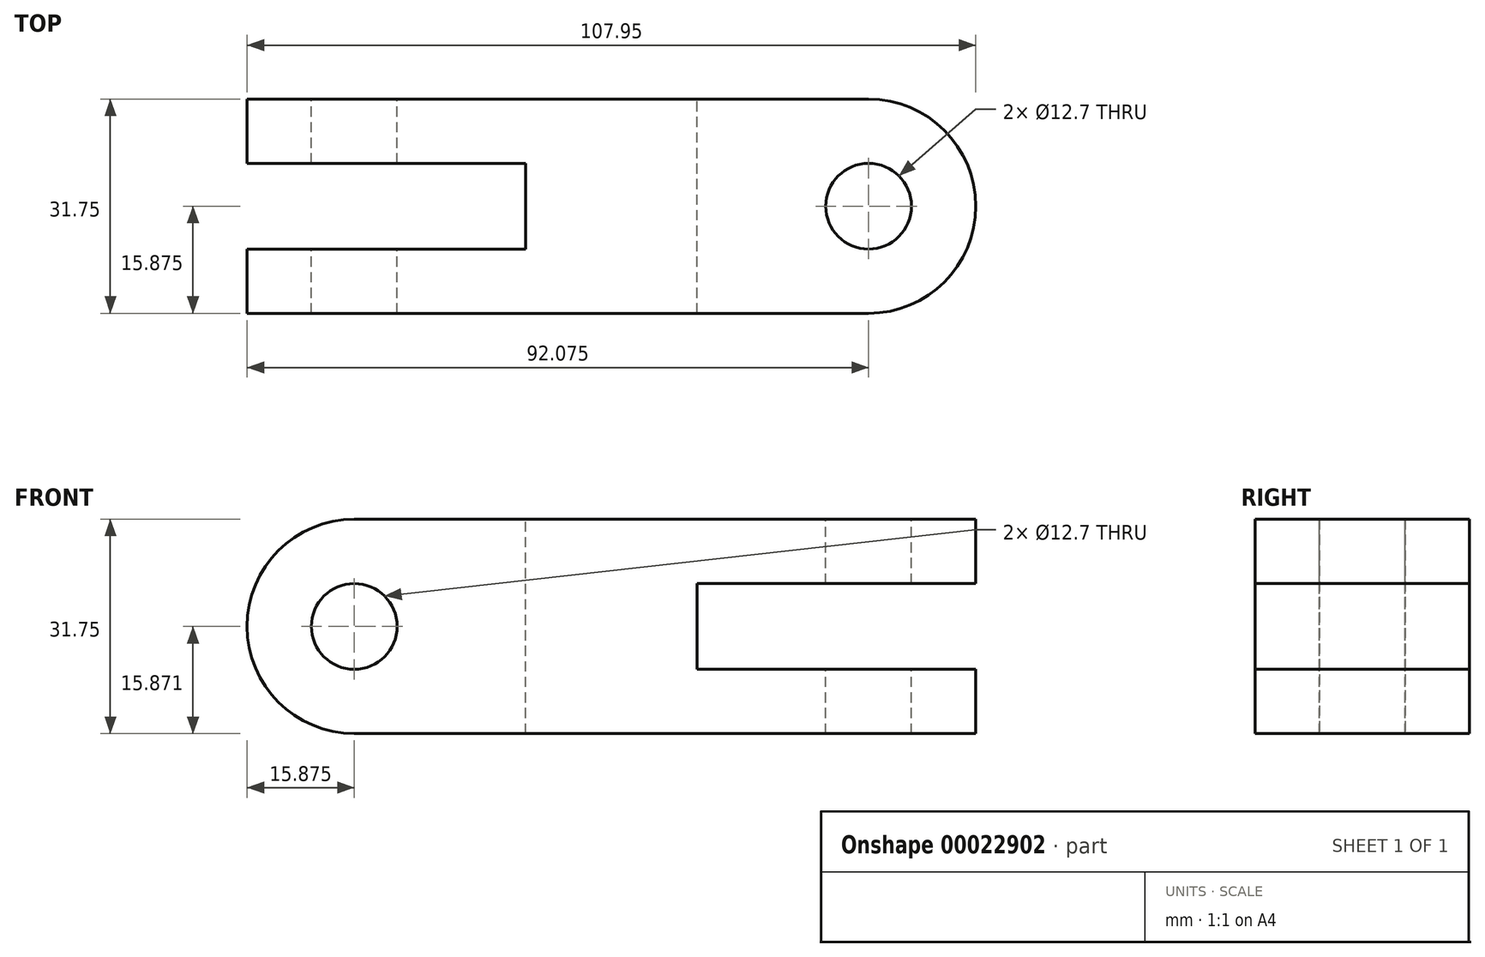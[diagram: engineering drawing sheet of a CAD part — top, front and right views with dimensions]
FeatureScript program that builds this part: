
annotation { "Feature Type Name" : "Feature", "Feature Type Description" : "" }
export const myFeature = defineFeature(function(context is Context, id is Id, definition is map)
    precondition{}
    {
        {
            var Q0;
            Q0=qCreatedBy(makeId("Front.planeOp"),FACE);
            var sketch = newSketch(context, id + "F0", { "sketchPlane" : qUnion([Q0])});
            skLineSegment(sketch, "E0.bottom", {"start": v(-92.08, 13.6) * mm, "end": v(0, 13.6) * mm});
            skLineSegment(sketch, "E0.top", {"start": v(-92.08, -18.14) * mm, "end": v(0, -18.14) * mm});
            skArc(sketch, "E1", {"start": v(-92.08, 13.6) * mm, "mid": v(-107.95, -2.27) * mm, "end": v(-92.08, -18.14) * mm});
            skCircle(sketch, "E2", {"center": v(-92.08, -2.27) * mm, "radius": 6.35 * mm});
            skLineSegment(sketch, "E3", {"start": v(0, 13.6) * mm, "end": v(0, 4.08) * mm});
            skLineSegment(sketch, "E4.0", {"start": v(-41.28, 4.08) * mm, "end": v(0, 4.08) * mm});
            skLineSegment(sketch, "E5.0", {"start": v(-41.28, -8.62) * mm, "end": v(0, -8.62) * mm});
            skLineSegment(sketch, "E6.0", {"start": v(-41.28, 4.08) * mm, "end": v(-41.28, -8.62) * mm});
            skLineSegment(sketch, "E7.trimOffspring", {"start": v(0, -8.62) * mm, "end": v(0, -18.14) * mm});
            skSolve(sketch);
        }
        {
            var Q0;
            Q0 = qSketchRegion(id + "F0", true);
            extrude(context, id + "F1", {"entities" : qUnion([Q0]), "depth" : 31.75 * mm});
        }
        {
            var Q0;
            Q0=makeQuery(id+"F1.opExtrude","SWEPT_FACE",FACE,{"disambiguationData":[OSD([sQuery(id+"F0.wireOp",EDGE,"E0.bottom")])]});
            var sketch = newSketch(context, id + "F2", { "sketchPlane" : qUnion([Q0])});
            skCircle(sketch, "E8", {"center": v(-15.88, -15.88) * mm, "radius": 6.35 * mm});
            skArc(sketch, "E9", {"start": v(-15.88, -31.75) * mm, "mid": v(0, -15.88) * mm, "end": v(-15.87, 0) * mm});
            skLineSegment(sketch, "E10", {"start": v(-92.08, -31.75) * mm, "end": v(-107.95, -31.75) * mm});
            skLineSegment(sketch, "E11.bottom", {"start": v(-107.95, -31.75) * mm, "end": v(-92.08, -31.75) * mm});
            skLineSegment(sketch, "E11.left", {"start": v(-107.95, -31.75) * mm, "end": v(-107.95, -9.52) * mm});
            skLineSegment(sketch, "E12.0", {"start": v(-107.95, -22.23) * mm, "end": v(-92.08, -22.23) * mm});
            skLineSegment(sketch, "E13.0", {"start": v(-107.95, -9.53) * mm, "end": v(-92.08, -9.53) * mm});
            skLineSegment(sketch, "E14.0", {"start": v(-66.67, -22.23) * mm, "end": v(-66.67, -9.53) * mm});
            skLineSegment(sketch, "E15.bottom", {"start": v(-92.08, -9.53) * mm, "end": v(-66.67, -9.53) * mm});
            skLineSegment(sketch, "E15.top", {"start": v(-92.08, -22.23) * mm, "end": v(-66.67, -22.23) * mm});
            skLineSegment(sketch, "E15.right", {"start": v(-66.67, -9.53) * mm, "end": v(-66.67, -22.23) * mm});
            skLineSegment(sketch, "E16.bottom", {"start": v(-15.88, 0) * mm, "end": v(0, 0) * mm});
            skLineSegment(sketch, "E16.top", {"start": v(-15.88, -31.75) * mm, "end": v(0, -31.75) * mm});
            skLineSegment(sketch, "E16.right", {"start": v(0, 0) * mm, "end": v(0, -31.75) * mm});
            skSolve(sketch);
        }
        {
            var Q0;
            Q0 = qSketchRegion(id + "F2", true);
            extrude(context, id + "F3", {"entities" : qUnion([Q0]), "operationType" : NewBodyOperationType.REMOVE, "oppositeDirection" : true, "depth" : 66.39 * mm});
        }
    });
